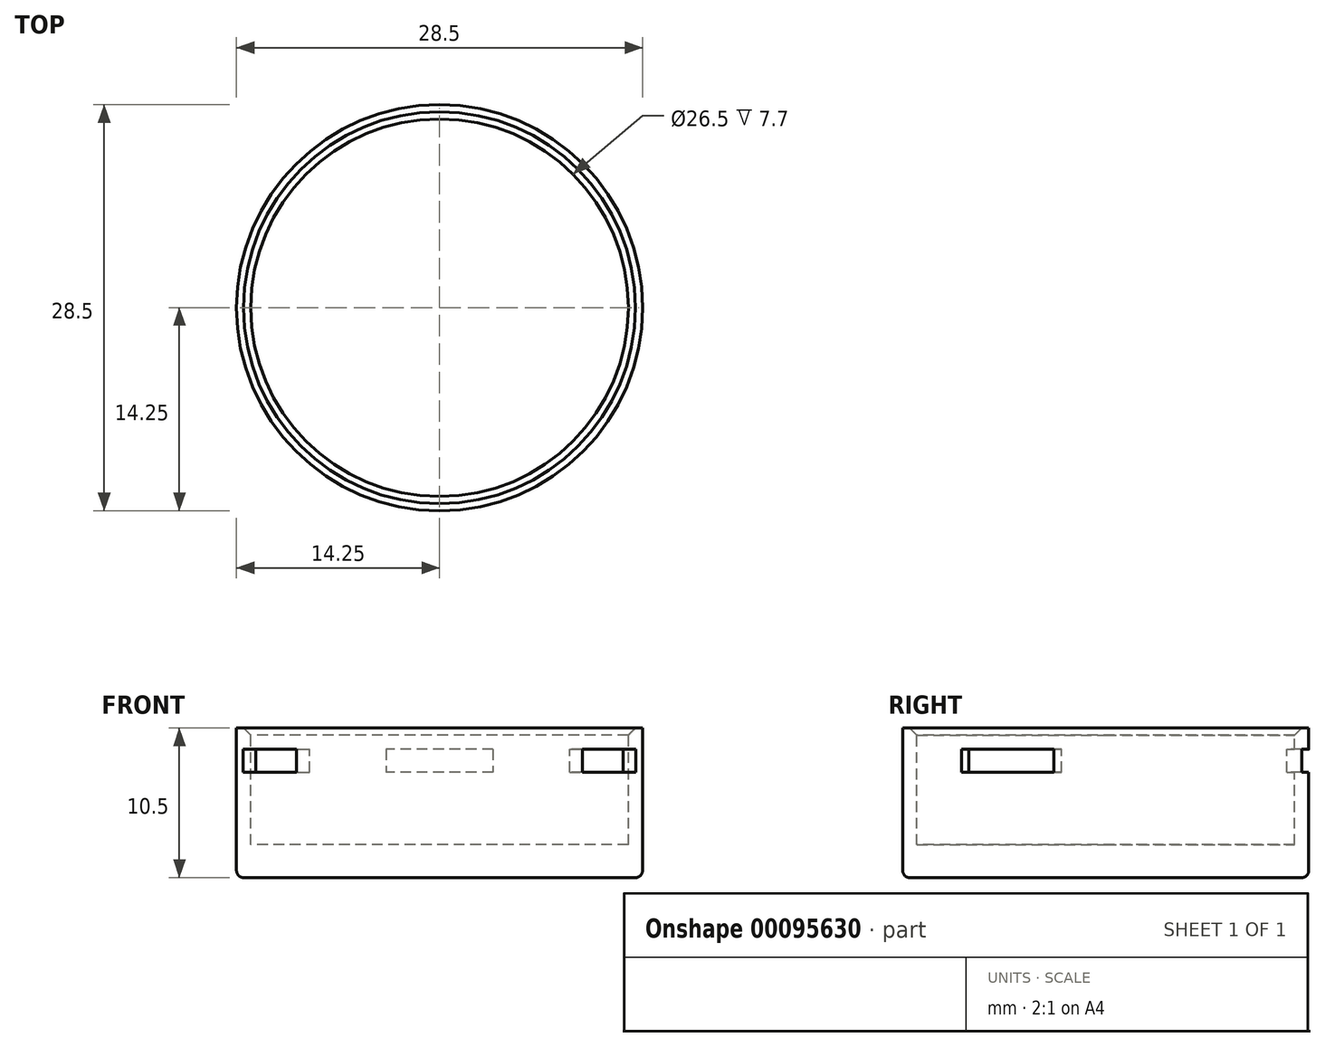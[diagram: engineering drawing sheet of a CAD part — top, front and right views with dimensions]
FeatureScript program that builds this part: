
annotation { "Feature Type Name" : "Feature", "Feature Type Description" : "" }
export const myFeature = defineFeature(function(context is Context, id is Id, definition is map)
    precondition{}
    {
        {
            var Q0;
            Q0=qCreatedBy(makeId("Top.planeOp"),FACE);
            var sketch = newSketch(context, id + "F0", { "sketchPlane" : qUnion([Q0])});
            skCircle(sketch, "E0", {"center": v(0, 0) * mm, "radius": 14.25 * mm});
            skSolve(sketch);
        }
        {
            var Q0;
            Q0=qSketchRegion(id+"F0",true);
            extrude(context, id + "F1", {"entities" : qUnion([Q0]), "depth" : 9 * mm});
        }
        {
            var Q0;
            Q0=makeQuery(id+"F1.opExtrude","CAP_FACE",FACE,{"disambiguationData":[OSD([sQuery(id+"F0.wireOp",EDGE,"E0")])],"isStart":false});
            var sketch = newSketch(context, id + "F2", { "sketchPlane" : qUnion([Q0])});
            skCircle(sketch, "E1", {"center": v(0, 0) * mm, "radius": 13.25 * mm});
            skSolve(sketch);
        }
        {
            var Q0;
            Q0=qSketchRegion(id+"F2",true);
            extrude(context, id + "F3", {"entities" : qUnion([Q0]), "operationType" : NewBodyOperationType.REMOVE, "oppositeDirection" : true, "depth" : 6.7 * mm});
        }
        {
            var Q0;
            Q0=makeQuery(id+"F1.opExtrude","CAP_EDGE",EDGE,{"disambiguationData":[OSD([sQuery(id+"F0.wireOp",EDGE,"E0")])],"isStart":true});
            fillet(context, id + "F4", {"entities" : qUnion([Q0]), "radius" : .5 * mm, "tangentPropagation" : true, "allowEdgeOverflow" : false});
        }
        {
            var Q0;
            Q0=makeQuery(id+"F1.opExtrude","CAP_FACE",FACE,{"disambiguationData":[OSD([sQuery(id+"F0.wireOp",EDGE,"E0")])],"isStart":false});
            var sketch = newSketch(context, id + "F5", { "sketchPlane" : qUnion([Q0])});
            skLineSegment(sketch, "E2", {"start": v(-3.75, 14.94) * mm, "end": v(-3.75, 11.65) * mm});
            skLineSegment(sketch, "E3", {"start": v(3.75, 14.94) * mm, "end": v(3.75, 11.65) * mm});
            skLineSegment(sketch, "E4", {"start": v(-3.75, 14.94) * mm, "end": v(3.75, 14.94) * mm});
            skLineSegment(sketch, "E5", {"start": v(-3.75, 11.65) * mm, "end": v(3.75, 11.65) * mm});
            skLineSegment(sketch, "E6.1.0", {"start": v(-11.07, -10.72) * mm, "end": v(-8.21, -9.07) * mm});
            skLineSegment(sketch, "E6.1.1", {"start": v(-14.82, -4.22) * mm, "end": v(-11.96, -2.58) * mm});
            skLineSegment(sketch, "E6.1.2", {"start": v(-11.07, -10.72) * mm, "end": v(-14.82, -4.22) * mm});
            skLineSegment(sketch, "E6.1.3", {"start": v(-8.21, -9.07) * mm, "end": v(-11.96, -2.58) * mm});
            skLineSegment(sketch, "E6.2.0", {"start": v(14.82, -4.22) * mm, "end": v(11.96, -2.58) * mm});
            skLineSegment(sketch, "E6.2.1", {"start": v(11.07, -10.72) * mm, "end": v(8.21, -9.07) * mm});
            skLineSegment(sketch, "E6.2.2", {"start": v(14.82, -4.22) * mm, "end": v(11.07, -10.72) * mm});
            skLineSegment(sketch, "E6.2.3", {"start": v(11.96, -2.58) * mm, "end": v(8.21, -9.07) * mm});
            skPoint(sketch, "E6.center", {"position": v(0, 0) * mm});
            skSolve(sketch);
        }
        {
            var Q0;
            Q0=qSketchRegion(id+"F5",true);
            extrude(context, id + "F6", {"entities" : qUnion([Q0]), "operationType" : NewBodyOperationType.REMOVE, "oppositeDirection" : true, "depth" : 1.6 * mm});
        }
        {
            var Q0;
            {var subQ0=sQuery(id+"F0.wireOp",EDGE,"E0");Q0=makeQuery(id+"F6.boolean.opBoolean","SPLIT",FACE,{"disambiguationData":[TD([makeQuery(id+"F6.opExtrude","SWEPT_FACE",FACE,{"disambiguationData":[OSD([sQuery(id+"F5.wireOp",EDGE,"E2")])]})])],"derivedFrom":makeQuery(id+"F1.opExtrude","CAP_FACE",FACE,{"disambiguationData":[OSD([subQ0])],"isStart":false})});}
            var sketch = newSketch(context, id + "F7", { "sketchPlane" : qUnion([Q0])});
            skCircle(sketch, "E7", {"center": v(0, 0) * mm, "radius": 13.25 * mm});
            skCircle(sketch, "E8", {"center": v(0, 0) * mm, "radius": 14.25 * mm});
            skSolve(sketch);
        }
        {
            var Q0;
            Q0=qSketchRegion(id+"F7",true);
            extrude(context, id + "F8", {"entities" : qUnion([Q0]), "operationType" : NewBodyOperationType.ADD, "depth" : 1.5 * mm});
        }
        {
            var Q0;
            Q0=makeQuery(id+"F8.opExtrude","CAP_EDGE",EDGE,{"disambiguationData":[OSD([sQuery(id+"F7.wireOp",EDGE,"E7")])],"isStart":false});
            chamfer(context, id + "F9", {"entities" : qUnion([Q0]), "width" : .5 * mm, "tangentPropagation" : true});
        }
    });
